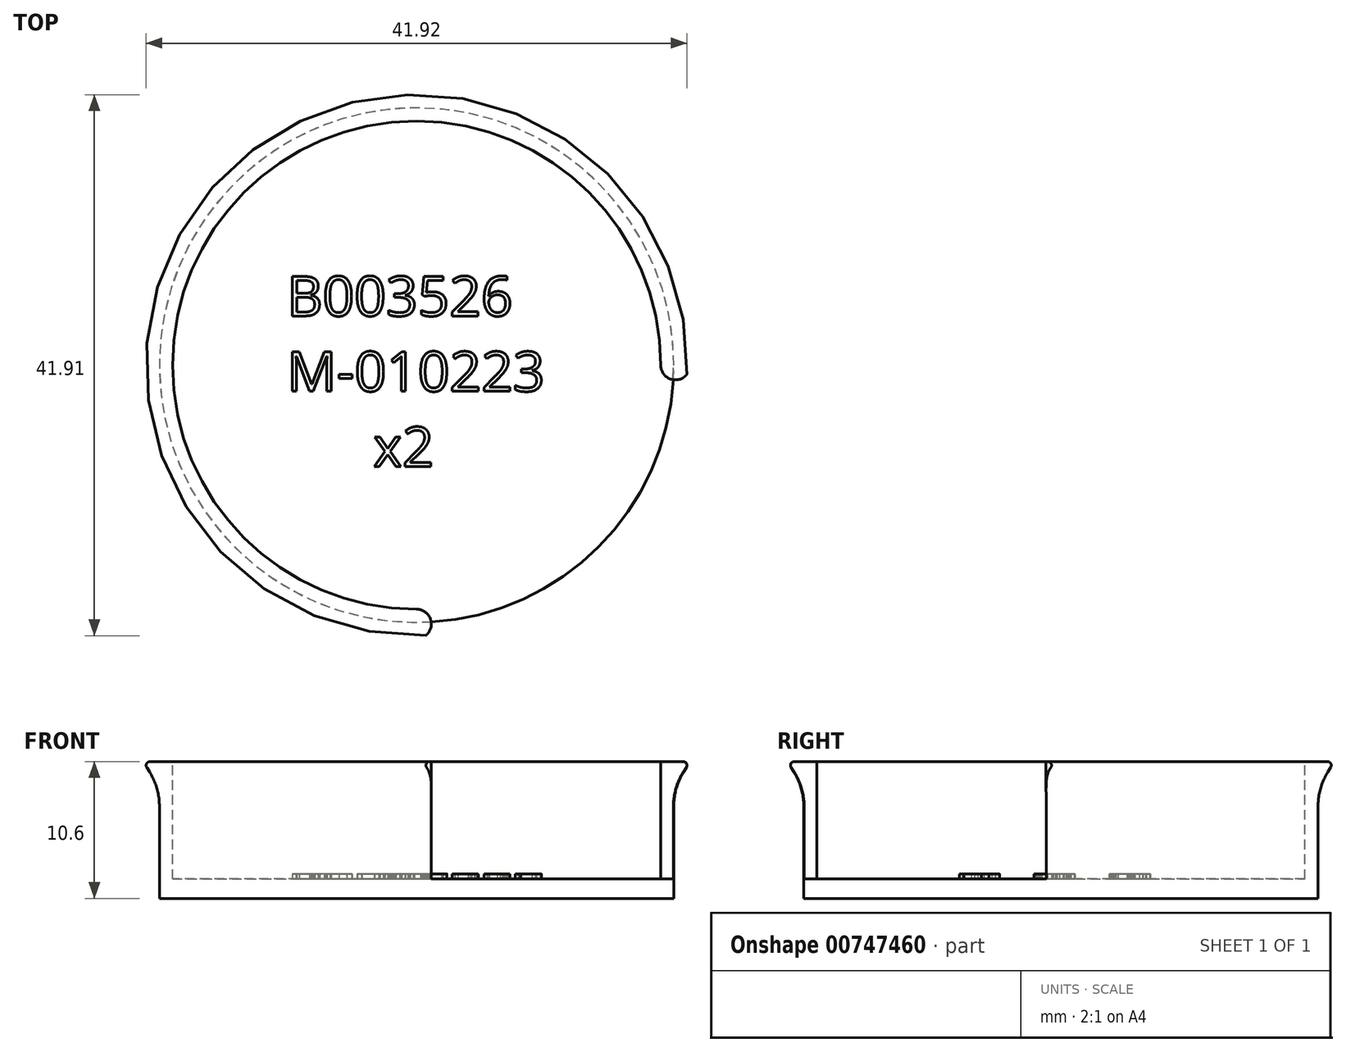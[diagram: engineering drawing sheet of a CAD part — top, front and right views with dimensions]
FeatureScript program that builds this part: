
annotation { "Feature Type Name" : "Feature", "Feature Type Description" : "" }
export const myFeature = defineFeature(function(context is Context, id is Id, definition is map)
    precondition{}
    {
        {
            var Q0;
            Q0=qCreatedBy(makeId("Right.planeOp"),FACE);
            var sketch = newSketch(context, id + "F0", { "sketchPlane" : qUnion([Q0])});
            skLineSegment(sketch, "E0", {"start": v(-36.1, 9.6) * mm, "end": v(-36.1, 0) * mm});
            skLineSegment(sketch, "E1", {"start": v(-36.1, 9.6) * mm, "end": v(-57.3, 9.6) * mm});
            skLineSegment(sketch, "E2", {"start": v(-36.1, 0) * mm, "end": v(-56.03, 0) * mm});
            skLineSegment(sketch, "E3", {"start": v(-56.03, 0) * mm, "end": v(-56.03, 7.57) * mm});
            skLineSegment(sketch, "E4", {"start": v(-56.03, 7.57) * mm, "end": v(-56.03, 9.6) * mm});
            skLineSegment(sketch, "E5", {"start": v(-57.3, 9.6) * mm, "end": v(-56.03, 7.57) * mm});
            skSolve(sketch);
        }
        {
            var Q0;
            Q0=qSketchRegion(id+"F0",true);
            var Q1;
            Q1=sQuery(id+"F0.wireOp",EDGE,"E0");
            revolve(context, id + "F1", {"entities" : qUnion([Q0]), "axis" : qUnion([Q1]), "revolveType" : RevolveType.FULL});
        }
        {
            var Q0;
            Q0=makeQuery(id+"F1.opRevolve","SWEPT_FACE",FACE,{"disambiguationData":[OSD([sQuery(id+"F0.wireOp",EDGE,"E1")])]});
            var sketch = newSketch(context, id + "F2", { "sketchPlane" : qUnion([Q0])});
            skCircle(sketch, "E6", {"center": v(0, -36.1) * mm, "radius": 18.91 * mm});
            skLineSegment(sketch, "E7.bottom", {"start": v(0, -36.1) * mm, "end": v(21.2, -36.1) * mm});
            skLineSegment(sketch, "E7.top", {"start": v(0, -57.3) * mm, "end": v(21.2, -57.3) * mm});
            skLineSegment(sketch, "E7.left", {"start": v(0, -36.1) * mm, "end": v(0, -57.3) * mm});
            skLineSegment(sketch, "E7.right", {"start": v(21.2, -36.1) * mm, "end": v(21.2, -57.3) * mm});
            skArc(sketch, "E8", {"start": v(0, -57.3) * mm, "mid": v(1.14, -56.15) * mm, "end": v(0, -55.01) * mm});
            skArc(sketch, "E9", {"start": v(18.91, -36.1) * mm, "mid": v(20.05, -37.24) * mm, "end": v(21.2, -36.1) * mm});
            skSolve(sketch);
        }
        {
            var Q0;
            {var subQ0=sQuery(id+"F2.wireOp",EDGE,"E7.left");var subQ3=sQuery(id+"F2.wireOp",EDGE,"E7.bottom");var subQ5=makeQuery(id+"F2.imprint","INTERSECT",VERTEX,{"derivedFrom":[subQ3,subQ0]});Q0=makeQuery(id+"F2.imprint","IMPRINT",FACE,{"disambiguationData":[TD([[makeQuery(id+"F2.imprint","IMPRINT",EDGE,{"disambiguationData":[TD([[subQ5,-1.0]])],"derivedFrom":subQ3}),1.0]])]});}
            var Q1;
            {var subQ0=sQuery(id+"F2.wireOp",EDGE,"E7.left");var subQ3=sQuery(id+"F2.wireOp",EDGE,"E7.bottom");var subQ5=makeQuery(id+"F2.imprint","INTERSECT",VERTEX,{"derivedFrom":[subQ3,subQ0]});Q1=makeQuery(id+"F2.imprint","IMPRINT",FACE,{"disambiguationData":[TD([[makeQuery(id+"F2.imprint","IMPRINT",EDGE,{"disambiguationData":[TD([[subQ5,-1.0]])],"derivedFrom":subQ3}),-1.0]])]});}
            var Q2;
            {var subQ0=sQuery(id+"F2.wireOp",EDGE,"E8");Q2=makeQuery(id+"F2.imprint","IMPRINT",FACE,{"disambiguationData":[TD([[makeQuery(id+"F2.imprint","IMPRINT",EDGE,{"derivedFrom":subQ0}),-1.0]])]});}
            extrude(context, id + "F3", {"entities" : qUnion([Q0, Q1, Q2]), "operationType" : NewBodyOperationType.REMOVE, "oppositeDirection" : true, "depth" : 9.1 * mm});
        }
        {
            var Q0;
            Q0=makeQuery(id+"F1.opRevolve","SWEPT_EDGE",EDGE,{"disambiguationData":[OSD([sQuery(id+"F0.wireOp",EDGE,"E1"),sQuery(id+"F0.wireOp",EDGE,"E5")])]});
            var Q1;
            Q1=makeQuery(id+"F3.boolean.opBoolean","COPY",EDGE,{"derivedFrom":makeQuery(id+"F3.opExtrude","CAP_EDGE",EDGE,{"disambiguationData":[OSD([sQuery(id+"F2.wireOp",EDGE,"E6")])],"isStart":true})});
            fillet(context, id + "F4", {"entities" : qUnion([Q0, Q1]), "radius" : 0.3 * mm, "tangentPropagation" : true, "allowEdgeOverflow" : false});
        }
        {
            var Q0;
            Q0=makeQuery(id+"F1.opRevolve","SWEPT_EDGE",EDGE,{"disambiguationData":[OSD([sQuery(id+"F0.wireOp",EDGE,"E3"),sQuery(id+"F0.wireOp",EDGE,"E4"),sQuery(id+"F0.wireOp",EDGE,"E5")])]});
            fillet(context, id + "F5", {"entities" : qUnion([Q0]), "radius" : 5 * mm, "tangentPropagation" : true, "allowEdgeOverflow" : false});
        }
        {
            var Q0;
            Q0=makeQuery(id+"F3.boolean.opBoolean","COPY",FACE,{"derivedFrom":makeQuery(id+"F3.opExtrude","CAP_FACE",FACE,{"disambiguationData":[OSD([sQuery(id+"F0.wireOp",EDGE,"E1"),sQuery(id+"F0.wireOp",EDGE,"E5"),sQuery(id+"F2.wireOp",EDGE,"E6"),sQuery(id+"F2.wireOp",EDGE,"E8"),sQuery(id+"F2.wireOp",EDGE,"E9")])],"isStart":false})});
            var sketch = newSketch(context, id + "F6", { "sketchPlane" : qUnion([Q0])});
            skText(sketch, "E10", { "text": "B003526\nM-010223\n      x2", "fontName": "OpenSans-Regular.ttf"});
            const initialGuessF6  = {"E10": [-0.01006, -0.03229, 1, 0, 0.00309]};
            skSetInitialGuess(sketch, initialGuessF6);
            skSolve(sketch);
        }
        {
            var Q0;
            Q0=qSketchRegion(id+"F6",true);
            extrude(context, id + "F7", {"entities" : qUnion([Q0]), "operationType" : NewBodyOperationType.ADD, "depth" : 0.4 * mm, "offsetDistance" : 25 * mm});
        }
        {
            var Q0;
            Q0=makeQuery(id+"F1.opRevolve","SWEPT_FACE",FACE,{"disambiguationData":[OSD([sQuery(id+"F0.wireOp",EDGE,"E2")])]});
            extrude(context, id + "F8", {"entities" : qUnion([Q0]), "operationType" : NewBodyOperationType.ADD, "depth" : 1 * mm, "offsetDistance" : 25 * mm});
        }
    });
